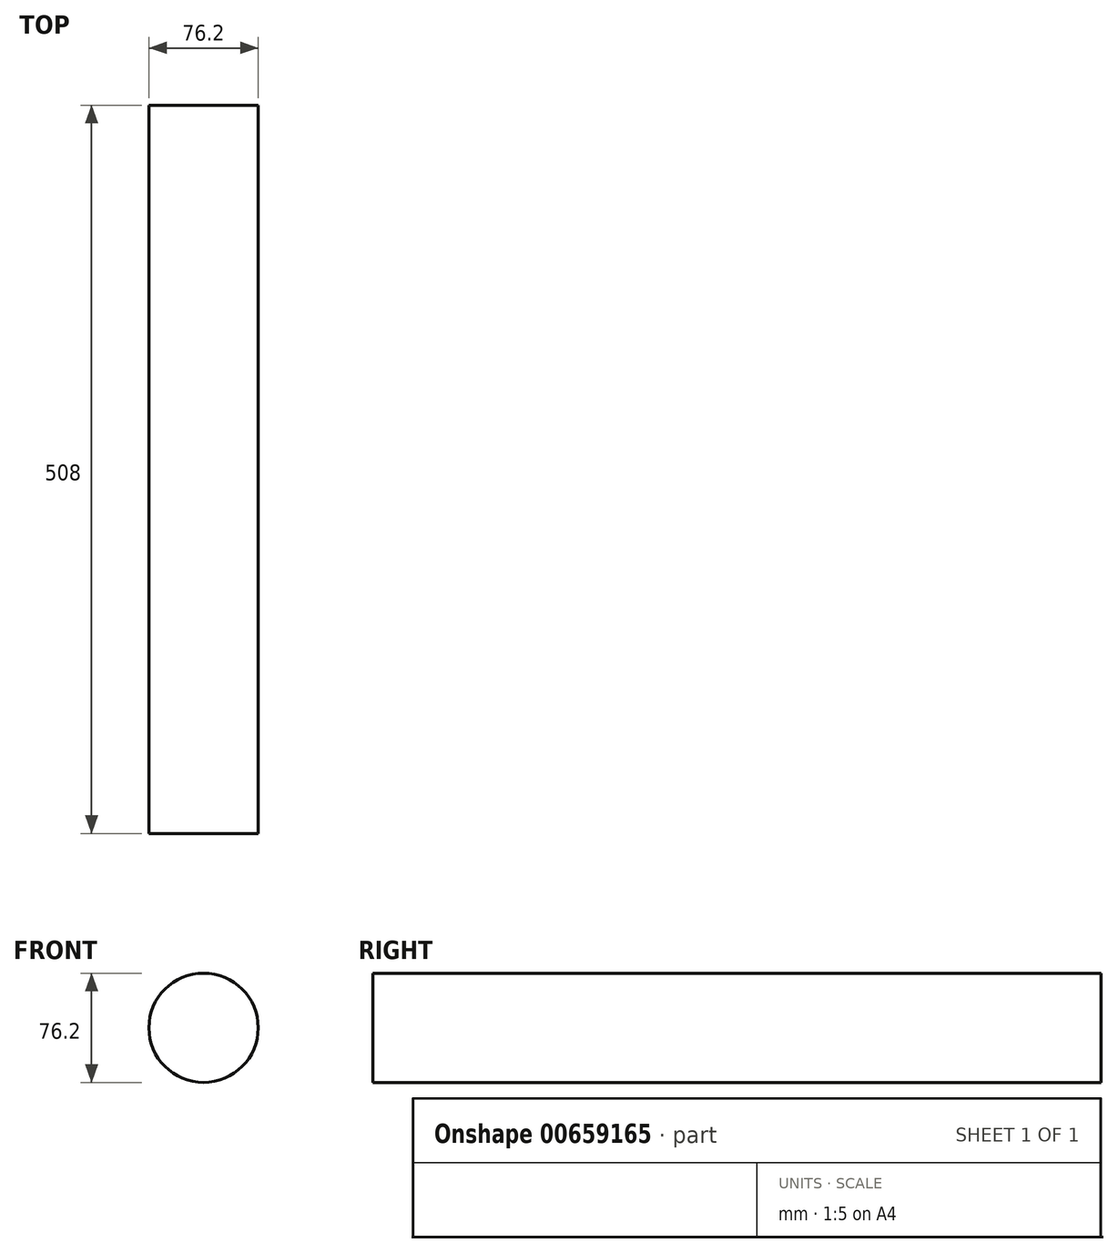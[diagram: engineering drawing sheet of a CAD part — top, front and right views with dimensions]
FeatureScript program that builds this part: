
annotation { "Feature Type Name" : "Feature", "Feature Type Description" : "" }
export const myFeature = defineFeature(function(context is Context, id is Id, definition is map)
    precondition{}
    {
        {
            var Q0;
            Q0=qCreatedBy(makeId("Front.planeOp"),FACE);
            var sketch = newSketch(context, id + "F0", { "sketchPlane" : qUnion([Q0])});
            skCircle(sketch, "E0", {"center": v(0, 0) * mm, "radius": 38.1 * mm});
            skSolve(sketch);
        }
        {
            var Q0;
            Q0 = qSketchRegion(id + "F0", true);
            extrude(context, id + "F1", {"entities" : qUnion([Q0]), "depth" : 508 * mm, "offsetDistance" : 25.4 * mm});
        }
    });
